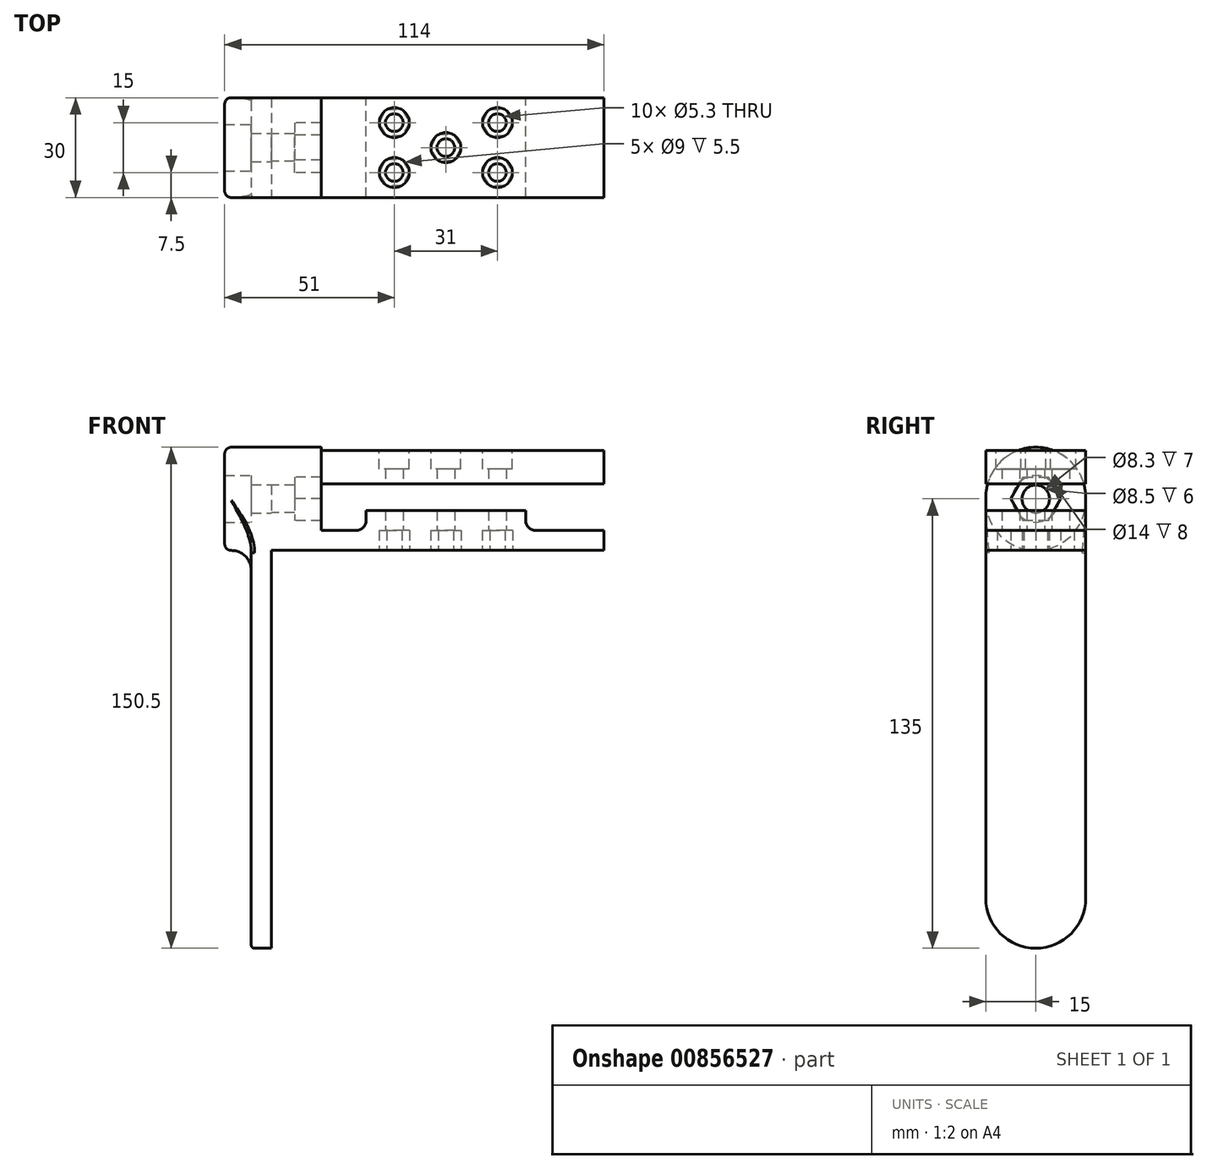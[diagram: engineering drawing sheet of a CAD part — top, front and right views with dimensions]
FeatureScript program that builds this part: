
annotation { "Feature Type Name" : "Feature", "Feature Type Description" : "" }
export const myFeature = defineFeature(function(context is Context, id is Id, definition is map)
    precondition{}
    {
        {
            var Q0;
            Q0=qCreatedBy(makeId("Top.planeOp"),FACE);
            var sketch = newSketch(context, id + "F0", { "sketchPlane" : qUnion([Q0])});
            skLineSegment(sketch, "E0.bottom", {"start": v(-50, 15) * mm, "end": v(50, 15) * mm});
            skLineSegment(sketch, "E0.top", {"start": v(-50, -15) * mm, "end": v(50, -15) * mm});
            skLineSegment(sketch, "E0.left", {"start": v(-50, 15) * mm, "end": v(-50, -15) * mm});
            skLineSegment(sketch, "E0.right", {"start": v(50, 15) * mm, "end": v(50, -15) * mm});
            skLineSegment(sketch, "E1", {"start": v(-35, 15) * mm, "end": v(-35, -15) * mm});
            skCircle(sketch, "E2", {"center": v(-13, 7.5) * mm, "radius": 2.65 * mm});
            skCircle(sketch, "E3", {"center": v(18, 7.5) * mm, "radius": 2.65 * mm});
            skCircle(sketch, "E4", {"center": v(18, -7.5) * mm, "radius": 2.65 * mm});
            skCircle(sketch, "E5", {"center": v(-13, -7.5) * mm, "radius": 2.65 * mm});
            skCircle(sketch, "E6", {"center": v(2.5, 0) * mm, "radius": 2.65 * mm});
            skLineSegment(sketch, "E7.bottom", {"start": v(-21.5, 15) * mm, "end": v(26.5, 15) * mm});
            skLineSegment(sketch, "E7.top", {"start": v(-21.5, -15) * mm, "end": v(26.5, -15) * mm});
            skLineSegment(sketch, "E7.left", {"start": v(-21.5, 15) * mm, "end": v(-21.5, -15) * mm});
            skLineSegment(sketch, "E7.right", {"start": v(26.5, 15) * mm, "end": v(26.5, -15) * mm});
            skCircle(sketch, "E8.cCircle", {"center": v(-13, 7.5) * mm, "radius": 4 * mm, "construction": true});
            skLineSegment(sketch, "E8.0", {"start": v(-10.7, 3.5) * mm, "end": v(-15.3, 3.5) * mm});
            skLineSegment(sketch, "E8.1", {"start": v(-15.3, 3.5) * mm, "end": v(-17.62, 7.5) * mm});
            skLineSegment(sketch, "E8.2", {"start": v(-17.62, 7.5) * mm, "end": v(-15.3, 11.5) * mm});
            skLineSegment(sketch, "E8.3", {"start": v(-15.3, 11.5) * mm, "end": v(-10.7, 11.5) * mm});
            skLineSegment(sketch, "E8.4", {"start": v(-10.7, 11.5) * mm, "end": v(-8.38, 7.5) * mm});
            skLineSegment(sketch, "E8.5", {"start": v(-8.38, 7.5) * mm, "end": v(-10.7, 3.5) * mm});
            skPoint(sketch, "E8.0.midPoint", {"position": v(-13, 3.5) * mm});
            skCircle(sketch, "E9.cCircle", {"center": v(18, 7.5) * mm, "radius": 4 * mm, "construction": true});
            skLineSegment(sketch, "E9.0", {"start": v(20.3, 3.5) * mm, "end": v(15.7, 3.5) * mm});
            skLineSegment(sketch, "E9.1", {"start": v(15.7, 3.5) * mm, "end": v(13.38, 7.5) * mm});
            skLineSegment(sketch, "E9.2", {"start": v(13.38, 7.5) * mm, "end": v(15.7, 11.5) * mm});
            skLineSegment(sketch, "E9.3", {"start": v(15.7, 11.5) * mm, "end": v(20.3, 11.5) * mm});
            skLineSegment(sketch, "E9.4", {"start": v(20.3, 11.5) * mm, "end": v(22.62, 7.5) * mm});
            skLineSegment(sketch, "E9.5", {"start": v(22.62, 7.5) * mm, "end": v(20.3, 3.5) * mm});
            skPoint(sketch, "E9.0.midPoint", {"position": v(18, 3.5) * mm});
            skCircle(sketch, "E10.cCircle", {"center": v(-13, -7.5) * mm, "radius": 4 * mm, "construction": true});
            skLineSegment(sketch, "E10.0", {"start": v(-15.3, -3.5) * mm, "end": v(-10.7, -3.5) * mm});
            skLineSegment(sketch, "E10.1", {"start": v(-10.7, -3.5) * mm, "end": v(-8.38, -7.5) * mm});
            skLineSegment(sketch, "E10.2", {"start": v(-8.38, -7.5) * mm, "end": v(-10.7, -11.5) * mm});
            skLineSegment(sketch, "E10.3", {"start": v(-10.7, -11.5) * mm, "end": v(-15.3, -11.5) * mm});
            skLineSegment(sketch, "E10.4", {"start": v(-15.3, -11.5) * mm, "end": v(-17.62, -7.5) * mm});
            skLineSegment(sketch, "E10.5", {"start": v(-17.62, -7.5) * mm, "end": v(-15.3, -3.5) * mm});
            skPoint(sketch, "E10.0.midPoint", {"position": v(-13, -3.5) * mm});
            skCircle(sketch, "E11.cCircle", {"center": v(18, -7.5) * mm, "radius": 4 * mm, "construction": true});
            skLineSegment(sketch, "E11.0", {"start": v(15.7, -3.5) * mm, "end": v(20.3, -3.5) * mm});
            skLineSegment(sketch, "E11.1", {"start": v(20.3, -3.5) * mm, "end": v(22.62, -7.5) * mm});
            skLineSegment(sketch, "E11.2", {"start": v(22.62, -7.5) * mm, "end": v(20.3, -11.5) * mm});
            skLineSegment(sketch, "E11.3", {"start": v(20.3, -11.5) * mm, "end": v(15.7, -11.5) * mm});
            skLineSegment(sketch, "E11.4", {"start": v(15.7, -11.5) * mm, "end": v(13.38, -7.5) * mm});
            skLineSegment(sketch, "E11.5", {"start": v(13.38, -7.5) * mm, "end": v(15.7, -3.5) * mm});
            skPoint(sketch, "E11.0.midPoint", {"position": v(18, -3.5) * mm});
            skCircle(sketch, "E12.cCircle", {"center": v(2.5, 0) * mm, "radius": 4 * mm, "construction": true});
            skLineSegment(sketch, "E12.0", {"start": v(4.8, 4) * mm, "end": v(7.12, 0) * mm});
            skLineSegment(sketch, "E12.1", {"start": v(7.12, 0) * mm, "end": v(4.8, -4) * mm});
            skLineSegment(sketch, "E12.2", {"start": v(4.8, -4) * mm, "end": v(0.2, -4) * mm});
            skLineSegment(sketch, "E12.3", {"start": v(0.2, -4) * mm, "end": v(-2.12, 0) * mm});
            skLineSegment(sketch, "E12.4", {"start": v(-2.12, 0) * mm, "end": v(0.2, 4) * mm});
            skLineSegment(sketch, "E12.5", {"start": v(0.2, 4) * mm, "end": v(4.8, 4) * mm});
            skPoint(sketch, "E12.0.midPoint", {"position": v(5.96, 2) * mm});
            skSolve(sketch);
        }
        {
            var Q0;
            {var subQ0=sQuery(id+"F0.wireOp",EDGE,"E0.right");Q0=makeQuery(id+"F0.imprint","IMPRINT",FACE,{"disambiguationData":[TD([[makeQuery(id+"F0.imprint","IMPRINT",EDGE,{"derivedFrom":subQ0}),-1.0]])]});}
            var Q1;
            {var subQ2=sQuery(id+"F0.wireOp",EDGE,"E1");Q1=makeQuery(id+"F0.imprint","IMPRINT",FACE,{"disambiguationData":[TD([[makeQuery(id+"F0.imprint","IMPRINT",EDGE,{"derivedFrom":subQ2}),1.0]])]});}
            var Q2;
            Q2=makeQuery(id+"F0.imprint","IMPRINT",FACE,{"disambiguationData":[TD([[makeQuery(id+"F0.imprint","IMPRINT",EDGE,{"derivedFrom":sQuery(id+"F0.wireOp",EDGE,"E2")}),-1.0]])]});
            var Q3;
            Q3=makeQuery(id+"F0.imprint","IMPRINT",FACE,{"disambiguationData":[TD([[makeQuery(id+"F0.imprint","IMPRINT",EDGE,{"derivedFrom":sQuery(id+"F0.wireOp",EDGE,"E5")}),-1.0]])]});
            var Q4;
            Q4=makeQuery(id+"F0.imprint","IMPRINT",FACE,{"disambiguationData":[TD([[makeQuery(id+"F0.imprint","IMPRINT",EDGE,{"derivedFrom":sQuery(id+"F0.wireOp",EDGE,"E6")}),-1.0]])]});
            var Q5;
            Q5=makeQuery(id+"F0.imprint","IMPRINT",FACE,{"disambiguationData":[TD([[makeQuery(id+"F0.imprint","IMPRINT",EDGE,{"derivedFrom":sQuery(id+"F0.wireOp",EDGE,"E3")}),-1.0]])]});
            var Q6;
            {var subQ1=sQuery(id+"F0.wireOp",EDGE,"E7.left");Q6=makeQuery(id+"F0.imprint","IMPRINT",FACE,{"disambiguationData":[TD([[makeQuery(id+"F0.imprint","IMPRINT",EDGE,{"derivedFrom":subQ1}),1.0]])]});}
            var Q7;
            Q7=makeQuery(id+"F0.imprint","IMPRINT",FACE,{"disambiguationData":[TD([[makeQuery(id+"F0.imprint","IMPRINT",EDGE,{"derivedFrom":sQuery(id+"F0.wireOp",EDGE,"E4")}),-1.0]])]});
            extrude(context, id + "F1", {"entities" : qUnion([Q0, Q1, Q2, Q3, Q4, Q5, Q6, Q7]), "depth" : 6 * mm, "offsetDistance" : 25 * mm});
        }
        {
            var Q0;
            {var subQ1=sQuery(id+"F0.wireOp",EDGE,"E7.left");Q0=makeQuery(id+"F0.imprint","IMPRINT",FACE,{"disambiguationData":[TD([[makeQuery(id+"F0.imprint","IMPRINT",EDGE,{"derivedFrom":subQ1}),1.0]])]});}
            var Q1;
            Q1=makeQuery(id+"F0.imprint","IMPRINT",FACE,{"disambiguationData":[TD([[makeQuery(id+"F0.imprint","IMPRINT",EDGE,{"derivedFrom":sQuery(id+"F0.wireOp",EDGE,"E2")}),-1.0]])]});
            var Q2;
            Q2=makeQuery(id+"F0.imprint","IMPRINT",FACE,{"disambiguationData":[TD([[makeQuery(id+"F0.imprint","IMPRINT",EDGE,{"derivedFrom":sQuery(id+"F0.wireOp",EDGE,"E5")}),-1.0]])]});
            var Q3;
            Q3=makeQuery(id+"F0.imprint","IMPRINT",FACE,{"disambiguationData":[TD([[makeQuery(id+"F0.imprint","IMPRINT",EDGE,{"derivedFrom":sQuery(id+"F0.wireOp",EDGE,"E6")}),-1.0]])]});
            var Q4;
            Q4=makeQuery(id+"F0.imprint","IMPRINT",FACE,{"disambiguationData":[TD([[makeQuery(id+"F0.imprint","IMPRINT",EDGE,{"derivedFrom":sQuery(id+"F0.wireOp",EDGE,"E3")}),-1.0]])]});
            var Q5;
            Q5=makeQuery(id+"F0.imprint","IMPRINT",FACE,{"disambiguationData":[TD([[makeQuery(id+"F0.imprint","IMPRINT",EDGE,{"derivedFrom":sQuery(id+"F0.wireOp",EDGE,"E4")}),-1.0]])]});
            extrude(context, id + "F2", {"entities" : qUnion([Q0, Q1, Q2, Q3, Q4, Q5]), "operationType" : NewBodyOperationType.ADD, "depth" : 12 * mm, "offsetDistance" : 25 * mm});
        }
        {
            var Q0;
            Q0=makeQuery(id+"F0.imprint","IMPRINT",FACE,{"disambiguationData":[TD([[makeQuery(id+"F0.imprint","IMPRINT",EDGE,{"derivedFrom":sQuery(id+"F0.wireOp",EDGE,"E5")}),-1.0]])]});
            var Q1;
            Q1=makeQuery(id+"F0.imprint","IMPRINT",FACE,{"disambiguationData":[TD([[makeQuery(id+"F0.imprint","IMPRINT",EDGE,{"derivedFrom":sQuery(id+"F0.wireOp",EDGE,"E2")}),-1.0]])]});
            var Q2;
            Q2=makeQuery(id+"F0.imprint","IMPRINT",FACE,{"disambiguationData":[TD([[makeQuery(id+"F0.imprint","IMPRINT",EDGE,{"derivedFrom":sQuery(id+"F0.wireOp",EDGE,"E6")}),-1.0]])]});
            var Q3;
            Q3=makeQuery(id+"F0.imprint","IMPRINT",FACE,{"disambiguationData":[TD([[makeQuery(id+"F0.imprint","IMPRINT",EDGE,{"derivedFrom":sQuery(id+"F0.wireOp",EDGE,"E4")}),-1.0]])]});
            var Q4;
            Q4=makeQuery(id+"F0.imprint","IMPRINT",FACE,{"disambiguationData":[TD([[makeQuery(id+"F0.imprint","IMPRINT",EDGE,{"derivedFrom":sQuery(id+"F0.wireOp",EDGE,"E3")}),-1.0]])]});
            extrude(context, id + "F3", {"entities" : qUnion([Q0, Q1, Q2, Q3, Q4]), "operationType" : NewBodyOperationType.REMOVE, "depth" : 6 * mm, "offsetDistance" : 25 * mm});
        }
        {
            var Q0;
            {var subQ0=sQuery(id+"F0.wireOp",EDGE,"E0.left");Q0=makeQuery(id+"F0.imprint","IMPRINT",FACE,{"disambiguationData":[TD([[makeQuery(id+"F0.imprint","IMPRINT",EDGE,{"derivedFrom":subQ0}),1.0]])]});}
            extrude(context, id + "F4", {"entities" : qUnion([Q0]), "operationType" : NewBodyOperationType.ADD, "depth" : 31 * mm, "offsetDistance" : 25 * mm});
        }
        {
            var Q0;
            Q0=makeQuery(id+"F1.opExtrude","CAP_EDGE",EDGE,{"disambiguationData":[OSD([sQuery(id+"F0.wireOp",EDGE,"E1")])],"isStart":false});
            var Q1;
            Q1=makeQuery(id+"F2.boolean.opBoolean","INTERSECT",EDGE,{"derivedFrom":[makeQuery(id+"F1.opExtrude","CAP_FACE",FACE,{"disambiguationData":[OSD([sQuery(id+"F0.wireOp",EDGE,"E0.bottom"),sQuery(id+"F0.wireOp",EDGE,"E0.top"),sQuery(id+"F0.wireOp",EDGE,"E0.right"),sQuery(id+"F0.wireOp",EDGE,"E1"),sQuery(id+"F0.wireOp",EDGE,"E2"),sQuery(id+"F0.wireOp",EDGE,"E3"),sQuery(id+"F0.wireOp",EDGE,"E4"),sQuery(id+"F0.wireOp",EDGE,"E5"),sQuery(id+"F0.wireOp",EDGE,"E6")])],"isStart":false}),makeQuery(id+"F2.opExtrude","SWEPT_FACE",FACE,{"disambiguationData":[OSD([sQuery(id+"F0.wireOp",EDGE,"E7.right")])]})]});
            var Q2;
            Q2=makeQuery(id+"F2.boolean.opBoolean","INTERSECT",EDGE,{"derivedFrom":[makeQuery(id+"F1.opExtrude","CAP_FACE",FACE,{"disambiguationData":[OSD([sQuery(id+"F0.wireOp",EDGE,"E0.bottom"),sQuery(id+"F0.wireOp",EDGE,"E0.top"),sQuery(id+"F0.wireOp",EDGE,"E0.right"),sQuery(id+"F0.wireOp",EDGE,"E1"),sQuery(id+"F0.wireOp",EDGE,"E2"),sQuery(id+"F0.wireOp",EDGE,"E3"),sQuery(id+"F0.wireOp",EDGE,"E4"),sQuery(id+"F0.wireOp",EDGE,"E5"),sQuery(id+"F0.wireOp",EDGE,"E6")])],"isStart":false}),makeQuery(id+"F2.opExtrude","SWEPT_FACE",FACE,{"disambiguationData":[OSD([sQuery(id+"F0.wireOp",EDGE,"E7.left")])]})]});
            fillet(context, id + "F5", {"entities" : qUnion([Q0, Q1, Q2]), "radius" : 3 * mm, "tangentPropagation" : true, "allowEdgeOverflow" : false});
        }
        {
            var Q0;
            Q0=makeQuery(id+"F4.opExtrude","SWEPT_FACE",FACE,{"disambiguationData":[OSD([sQuery(id+"F0.wireOp",EDGE,"E0.left")])]});
            var sketch = newSketch(context, id + "F6", { "sketchPlane" : qUnion([Q0])});
            skLineSegment(sketch, "E13", {"start": v(-15, 31) * mm, "end": v(15, 0) * mm});
            skCircle(sketch, "E14", {"center": v(0, 15.5) * mm, "radius": 4.15 * mm});
            skCircle(sketch, "E15.cCircle", {"center": v(0, 15.5) * mm, "radius": 6.5 * mm, "construction": true});
            skLineSegment(sketch, "E15.0", {"start": v(3.75, 9) * mm, "end": v(-3.75, 9) * mm});
            skLineSegment(sketch, "E15.1", {"start": v(-3.75, 9) * mm, "end": v(-7.5, 15.5) * mm});
            skLineSegment(sketch, "E15.2", {"start": v(-7.5, 15.5) * mm, "end": v(-3.75, 22) * mm});
            skLineSegment(sketch, "E15.3", {"start": v(-3.75, 22) * mm, "end": v(3.75, 22) * mm});
            skLineSegment(sketch, "E15.4", {"start": v(3.75, 22) * mm, "end": v(7.5, 15.5) * mm});
            skLineSegment(sketch, "E15.5", {"start": v(7.5, 15.5) * mm, "end": v(3.75, 9) * mm});
            skPoint(sketch, "E15.0.midPoint", {"position": v(0, 9) * mm});
            skSolve(sketch);
        }
        {
            var Q0;
            {var subQ0=sQuery(id+"F6.wireOp",EDGE,"E14");var subQ1=sQuery(id+"F6.wireOp",EDGE,"E13");var subQ2=makeQuery(id+"F6.imprint","INTERSECT",VERTEX,{"disambiguationData":[OD(0.0)],"derivedFrom":[subQ1,subQ0]});Q0=makeQuery(id+"F6.imprint","IMPRINT",FACE,{"disambiguationData":[TD([[makeQuery(id+"F6.imprint","IMPRINT",EDGE,{"disambiguationData":[TD([[subQ2,-1.0]])],"derivedFrom":subQ1}),1.0]])]});}
            var Q1;
            {var subQ0=sQuery(id+"F6.wireOp",EDGE,"E14");var subQ1=sQuery(id+"F6.wireOp",EDGE,"E13");var subQ2=makeQuery(id+"F6.imprint","INTERSECT",VERTEX,{"disambiguationData":[OD(0.0)],"derivedFrom":[subQ1,subQ0]});Q1=makeQuery(id+"F6.imprint","IMPRINT",FACE,{"disambiguationData":[TD([[makeQuery(id+"F6.imprint","IMPRINT",EDGE,{"disambiguationData":[TD([[subQ2,-1.0]])],"derivedFrom":subQ1}),-1.0]])]});}
            extrude(context, id + "F7", {"entities" : qUnion([Q0, Q1]), "operationType" : NewBodyOperationType.REMOVE, "oppositeDirection" : true, "depth" : 20 * mm, "offsetDistance" : 25 * mm});
        }
        {
            var Q0;
            Q0=qSketchRegion(id+"F6",true);
            extrude(context, id + "F8", {"entities" : qUnion([Q0]), "operationType" : NewBodyOperationType.REMOVE, "oppositeDirection" : true, "depth" : 20 * mm, "offsetDistance" : 25 * mm, "hasSecondDirection" : true, "secondDirectionOppositeDirection" : true, "secondDirectionDepth" : 7 * mm});
        }
        {
            var Q0;
            Q0=makeQuery(id+"F4.opExtrude","CAP_EDGE",EDGE,{"disambiguationData":[OSD([sQuery(id+"F0.wireOp",EDGE,"E0.top")])],"isStart":false});
            var Q1;
            Q1=makeQuery(id+"F4.opExtrude","CAP_EDGE",EDGE,{"disambiguationData":[OSD([sQuery(id+"F0.wireOp",EDGE,"E0.bottom")])],"isStart":false});
            fillet(context, id + "F9", {"entities" : qUnion([Q0, Q1]), "radius" : 15 * mm, "tangentPropagation" : true, "allowEdgeOverflow" : false});
        }
        {
            var Q0;
            {var subQ2=sQuery(id+"F0.wireOp",EDGE,"E1");Q0=makeQuery(id+"F0.imprint","IMPRINT",FACE,{"disambiguationData":[TD([[makeQuery(id+"F0.imprint","IMPRINT",EDGE,{"derivedFrom":subQ2}),1.0]])]});}
            var Q1;
            {var subQ1=sQuery(id+"F0.wireOp",EDGE,"E7.left");Q1=makeQuery(id+"F0.imprint","IMPRINT",FACE,{"disambiguationData":[TD([[makeQuery(id+"F0.imprint","IMPRINT",EDGE,{"derivedFrom":subQ1}),1.0]])]});}
            var Q2;
            {var subQ0=sQuery(id+"F0.wireOp",EDGE,"E0.right");Q2=makeQuery(id+"F0.imprint","IMPRINT",FACE,{"disambiguationData":[TD([[makeQuery(id+"F0.imprint","IMPRINT",EDGE,{"derivedFrom":subQ0}),-1.0]])]});}
            var Q3;
            Q3=makeQuery(id+"F0.imprint","IMPRINT",FACE,{"disambiguationData":[TD([[makeQuery(id+"F0.imprint","IMPRINT",EDGE,{"derivedFrom":sQuery(id+"F0.wireOp",EDGE,"E4")}),-1.0]])]});
            var Q4;
            Q4=makeQuery(id+"F0.imprint","IMPRINT",FACE,{"disambiguationData":[TD([[makeQuery(id+"F0.imprint","IMPRINT",EDGE,{"derivedFrom":sQuery(id+"F0.wireOp",EDGE,"E3")}),-1.0]])]});
            var Q5;
            Q5=makeQuery(id+"F0.imprint","IMPRINT",FACE,{"disambiguationData":[TD([[makeQuery(id+"F0.imprint","IMPRINT",EDGE,{"derivedFrom":sQuery(id+"F0.wireOp",EDGE,"E6")}),-1.0]])]});
            var Q6;
            Q6=makeQuery(id+"F0.imprint","IMPRINT",FACE,{"disambiguationData":[TD([[makeQuery(id+"F0.imprint","IMPRINT",EDGE,{"derivedFrom":sQuery(id+"F0.wireOp",EDGE,"E5")}),-1.0]])]});
            var Q7;
            Q7=makeQuery(id+"F0.imprint","IMPRINT",FACE,{"disambiguationData":[TD([[makeQuery(id+"F0.imprint","IMPRINT",EDGE,{"derivedFrom":sQuery(id+"F0.wireOp",EDGE,"E2")}),-1.0]])]});
            extrude(context, id + "F10", {"entities" : qUnion([Q0, Q1, Q2, Q3, Q4, Q5, Q6, Q7]), "depth" : 30 * mm, "offsetDistance" : 25 * mm, "hasSecondDirection" : true, "secondDirectionOppositeDirection" : false, "secondDirectionDepth" : 20 * mm});
        }
        {
            var Q0;
            Q0=makeQuery(id+"F10.opExtrude","CAP_FACE",FACE,{"disambiguationData":[OSD([sQuery(id+"F0.wireOp",EDGE,"E0.bottom"),sQuery(id+"F0.wireOp",EDGE,"E0.top"),sQuery(id+"F0.wireOp",EDGE,"E0.right"),sQuery(id+"F0.wireOp",EDGE,"E1"),sQuery(id+"F0.wireOp",EDGE,"E2"),sQuery(id+"F0.wireOp",EDGE,"E3"),sQuery(id+"F0.wireOp",EDGE,"E4"),sQuery(id+"F0.wireOp",EDGE,"E5"),sQuery(id+"F0.wireOp",EDGE,"E6")])],"isStart":false});
            var sketch = newSketch(context, id + "F11", { "sketchPlane" : qUnion([Q0])});
            skCircle(sketch, "E16", {"center": v(-13, 7.5) * mm, "radius": 4.5 * mm});
            skCircle(sketch, "E17", {"center": v(18, 7.5) * mm, "radius": 4.5 * mm});
            skCircle(sketch, "E18", {"center": v(18, -7.5) * mm, "radius": 4.5 * mm});
            skCircle(sketch, "E19", {"center": v(-13, -7.5) * mm, "radius": 4.5 * mm});
            skCircle(sketch, "E20", {"center": v(2.5, 0) * mm, "radius": 4.5 * mm});
            skSolve(sketch);
        }
        {
            var Q0;
            Q0=makeQuery(id+"F11.imprint","IMPRINT",FACE,{"disambiguationData":[TD([[makeQuery(id+"F11.imprint","IMPRINT",EDGE,{"derivedFrom":sQuery(id+"F11.wireOp",EDGE,"E16")}),1.0]])]});
            var Q1;
            Q1=makeQuery(id+"F11.imprint","IMPRINT",FACE,{"disambiguationData":[TD([[makeQuery(id+"F11.imprint","IMPRINT",EDGE,{"derivedFrom":sQuery(id+"F11.wireOp",EDGE,"E19")}),1.0]])]});
            var Q2;
            Q2=makeQuery(id+"F11.imprint","IMPRINT",FACE,{"disambiguationData":[TD([[makeQuery(id+"F11.imprint","IMPRINT",EDGE,{"derivedFrom":sQuery(id+"F11.wireOp",EDGE,"E17")}),1.0]])]});
            var Q3;
            Q3=makeQuery(id+"F11.imprint","IMPRINT",FACE,{"disambiguationData":[TD([[makeQuery(id+"F11.imprint","IMPRINT",EDGE,{"derivedFrom":sQuery(id+"F11.wireOp",EDGE,"E18")}),1.0]])]});
            var Q4;
            Q4=makeQuery(id+"F11.imprint","IMPRINT",FACE,{"disambiguationData":[TD([[makeQuery(id+"F11.imprint","IMPRINT",EDGE,{"derivedFrom":sQuery(id+"F11.wireOp",EDGE,"E20")}),1.0]])]});
            extrude(context, id + "F12", {"entities" : qUnion([Q0, Q1, Q2, Q3, Q4]), "operationType" : NewBodyOperationType.REMOVE, "oppositeDirection" : true, "depth" : 5.5 * mm, "offsetDistance" : 25 * mm});
        }
        {
            var Q0;
            Q0=makeQuery(id+"F4.opExtrude","SWEPT_FACE",FACE,{"disambiguationData":[OSD([sQuery(id+"F0.wireOp",EDGE,"E0.left")])]});
            var sketch = newSketch(context, id + "F13", { "sketchPlane" : qUnion([Q0])});
            skLineSegment(sketch, "E21.bottom", {"start": v(-15, 31) * mm, "end": v(15, 31) * mm});
            skLineSegment(sketch, "E21.top", {"start": v(0, -119.5) * mm, "end": v(0, -119.5) * mm});
            skLineSegment(sketch, "E21.left", {"start": v(-15, 31) * mm, "end": v(-15, -104.5) * mm});
            skLineSegment(sketch, "E21.right", {"start": v(15, 31) * mm, "end": v(15, -104.5) * mm});
            skCircle(sketch, "E22", {"center": v(0, 15.5) * mm, "radius": 4.25 * mm});
            skCircle(sketch, "E23", {"center": v(0, 15.5) * mm, "radius": 7 * mm});
            skPoint(sketch, "E24.visualSharp", {"position": v(15, -119.5) * mm});
            skArc(sketch, "E24.filletArc", {"start": v(0, -119.5) * mm, "mid": v(10.6, -115.1) * mm, "end": v(15, -104.5) * mm});
            skPoint(sketch, "E25.visualSharp", {"position": v(-15, -119.5) * mm});
            skArc(sketch, "E25.filletArc", {"start": v(-15, -104.5) * mm, "mid": v(-10.6, -115.1) * mm, "end": v(0, -119.5) * mm});
            skLineSegment(sketch, "E26", {"start": v(-15, 0) * mm, "end": v(15, 0) * mm});
            skSolve(sketch);
        }
        {
            var Q0;
            Q0=makeQuery(id+"F13.imprint","IMPRINT",FACE,{"disambiguationData":[TD([[makeQuery(id+"F13.imprint","IMPRINT",EDGE,{"derivedFrom":sQuery(id+"F13.wireOp",EDGE,"E23")}),-1.0]])]});
            var Q1;
            {var subQ0=sQuery(id+"F13.wireOp",EDGE,"E24.filletArc");Q1=makeQuery(id+"F13.imprint","IMPRINT",FACE,{"disambiguationData":[TD([[makeQuery(id+"F13.imprint","IMPRINT",EDGE,{"derivedFrom":subQ0}),1.0]])]});}
            var Q2;
            Q2=makeQuery(id+"F13.imprint","IMPRINT",FACE,{"disambiguationData":[TD([[makeQuery(id+"F13.imprint","IMPRINT",EDGE,{"derivedFrom":sQuery(id+"F13.wireOp",EDGE,"E22")}),-1.0]])]});
            extrude(context, id + "F14", {"entities" : qUnion([Q0, Q1, Q2]), "depth" : 6 * mm, "offsetDistance" : 25 * mm});
        }
        {
            var Q0;
            Q0=makeQuery(id+"F13.imprint","IMPRINT",FACE,{"disambiguationData":[TD([[makeQuery(id+"F13.imprint","IMPRINT",EDGE,{"derivedFrom":sQuery(id+"F13.wireOp",EDGE,"E23")}),-1.0]])]});
            extrude(context, id + "F15", {"entities" : qUnion([Q0]), "operationType" : NewBodyOperationType.ADD, "depth" : (8 + 6) * mm, "offsetDistance" : 25 * mm});
        }
        {
            var Q0;
            Q0=makeQuery(id+"F15.opExtrude","SWEPT_EDGE",EDGE,{"disambiguationData":[OSD([sQuery(id+"F13.wireOp",EDGE,"E21.left"),sQuery(id+"F13.wireOp",EDGE,"E26")])]});
            var Q1;
            Q1=makeQuery(id+"F15.opExtrude","SWEPT_EDGE",EDGE,{"disambiguationData":[OSD([sQuery(id+"F13.wireOp",EDGE,"E21.right"),sQuery(id+"F13.wireOp",EDGE,"E26")])]});
            fillet(context, id + "F16", {"entities" : qUnion([Q0, Q1]), "radius" : 15 * mm, "allowEdgeOverflow" : false});
        }
        {
            var Q0;
            {var subQ0=sQuery(id+"F13.wireOp",EDGE,"E21.left");var subQ1=sQuery(id+"F13.wireOp",EDGE,"E21.right");var subQ2=sQuery(id+"F13.wireOp",EDGE,"E25.filletArc");var subQ3=sQuery(id+"F13.wireOp",EDGE,"E24.filletArc");var subQ4=sQuery(id+"F13.wireOp",EDGE,"E26");Q0=makeQuery(id+"F16.opFillet","BLEND_EDGE",EDGE,{"blendedFrom":[makeQuery(id+"F15.opExtrude","SWEPT_EDGE",EDGE,{"disambiguationData":[OSD([subQ0,subQ4])]}),makeQuery(id+"F15.boolean.opBoolean","SPLIT",FACE,{"disambiguationData":[TD([makeQuery(id+"F14.opExtrude","SWEPT_FACE",FACE,{"disambiguationData":[OSD([subQ0])]})])],"derivedFrom":makeQuery(id+"F14.opExtrude","CAP_FACE",FACE,{"disambiguationData":[OSD([sQuery(id+"F0.wireOp",EDGE,"E0.bottom"),sQuery(id+"F0.wireOp",EDGE,"E0.left"),subQ0,subQ1,sQuery(id+"F13.wireOp",EDGE,"E22"),subQ3,subQ2])],"isStart":false})})],"blendedInto":[makeQuery(id+"F15.boolean.opBoolean","SPLIT",FACE,{"disambiguationData":[TD([makeQuery(id+"F14.opExtrude","SWEPT_FACE",FACE,{"disambiguationData":[OSD([subQ0])]})])],"derivedFrom":makeQuery(id+"F14.opExtrude","CAP_FACE",FACE,{"disambiguationData":[OSD([sQuery(id+"F0.wireOp",EDGE,"E0.bottom"),sQuery(id+"F0.wireOp",EDGE,"E0.left"),subQ0,subQ1,sQuery(id+"F13.wireOp",EDGE,"E22"),subQ3,subQ2])],"isStart":false})})]});}
            fillet(context, id + "F17", {"entities" : qUnion([Q0]), "radius" : 6 * mm, "tangentPropagation" : true, "allowEdgeOverflow" : false});
        }
        {
            var Q0;
            {var subQ0=sQuery(id+"F13.wireOp",EDGE,"E26");var subQ1=sQuery(id+"F13.wireOp",EDGE,"E21.left");Q0=makeQuery(id+"F16.opFillet","BLEND_EDGE",EDGE,{"blendedFrom":[makeQuery(id+"F15.opExtrude","SWEPT_EDGE",EDGE,{"disambiguationData":[OSD([subQ1,subQ0])]}),makeQuery(id+"F15.opExtrude","CAP_FACE",FACE,{"disambiguationData":[OSD([sQuery(id+"F0.wireOp",EDGE,"E0.bottom"),sQuery(id+"F0.wireOp",EDGE,"E0.left"),subQ1,sQuery(id+"F13.wireOp",EDGE,"E21.right"),sQuery(id+"F13.wireOp",EDGE,"E23"),subQ0])],"isStart":false})],"blendedInto":[makeQuery(id+"F15.opExtrude","CAP_FACE",FACE,{"disambiguationData":[OSD([sQuery(id+"F0.wireOp",EDGE,"E0.bottom"),sQuery(id+"F0.wireOp",EDGE,"E0.left"),subQ1,sQuery(id+"F13.wireOp",EDGE,"E21.right"),sQuery(id+"F13.wireOp",EDGE,"E23"),subQ0])],"isStart":false})]});}
            fillet(context, id + "F18", {"entities" : qUnion([Q0]), "radius" : 2 * mm, "tangentPropagation" : true, "allowEdgeOverflow" : false});
        }
        {
            var Q0;
            Q0=makeQuery(id+"F14.opExtrude","CAP_EDGE",EDGE,{"disambiguationData":[OSD([sQuery(id+"F13.wireOp",EDGE,"E21.right")])],"isStart":false});
            fillet(context, id + "F19", {"entities" : qUnion([Q0]), "radius" : 1 * mm, "tangentPropagation" : true, "allowEdgeOverflow" : false});
        }
    });
